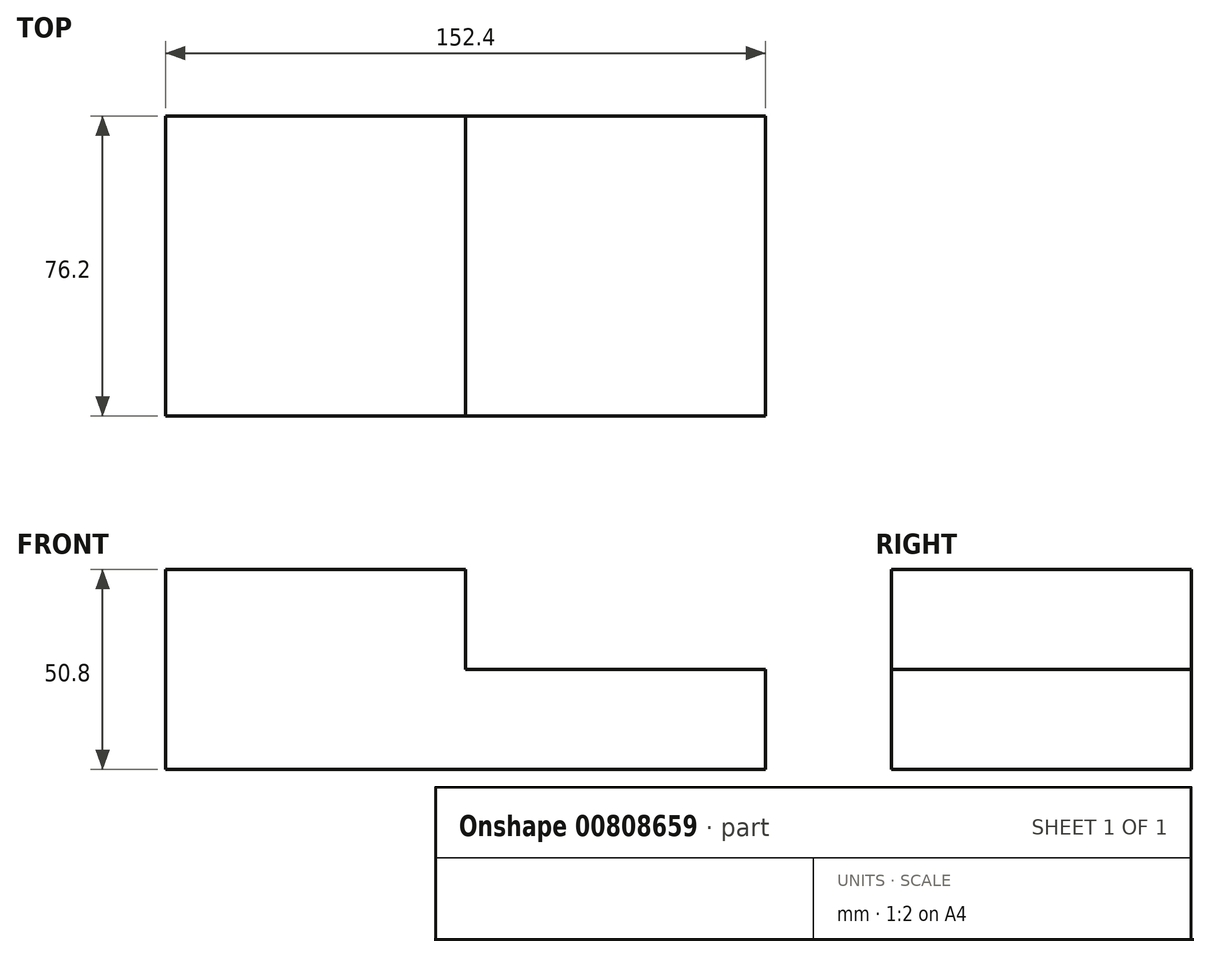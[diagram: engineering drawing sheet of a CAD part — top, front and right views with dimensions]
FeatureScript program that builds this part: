
annotation { "Feature Type Name" : "Feature", "Feature Type Description" : "" }
export const myFeature = defineFeature(function(context is Context, id is Id, definition is map)
    precondition{}
    {
        {
            var Q0;
            Q0=qCreatedBy(makeId("Front.planeOp"),FACE);
            var sketch = newSketch(context, id + "F0", { "sketchPlane" : qUnion([Q0])});
            skLineSegment(sketch, "E0", {"start": v(-72.41, 0) * mm, "end": v(79.99, 0) * mm});
            skLineSegment(sketch, "E1", {"start": v(-72.41, 0) * mm, "end": v(-72.41, 50.8) * mm});
            skLineSegment(sketch, "E2", {"start": v(-72.41, 50.8) * mm, "end": v(3.79, 50.8) * mm});
            skLineSegment(sketch, "E3", {"start": v(3.79, 50.8) * mm, "end": v(3.79, 25.4) * mm});
            skLineSegment(sketch, "E4", {"start": v(3.79, 25.4) * mm, "end": v(79.99, 25.4) * mm});
            skLineSegment(sketch, "E5", {"start": v(79.99, 25.4) * mm, "end": v(79.99, 0) * mm});
            skSolve(sketch);
        }
        {
            var Q0;
            Q0 = qSketchRegion(id + "F0", true);
            extrude(context, id + "F1", {"entities" : qUnion([Q0]), "depth" : 25.4 * mm, "offsetDistance" : 25.4 * mm});
        }
        {
            var Q0;
            Q0=makeQuery(id+"F1.opExtrude","CAP_FACE",FACE,{"disambiguationData":[OSD([sQuery(id+"F0.wireOp",EDGE,"E0"),sQuery(id+"F0.wireOp",EDGE,"E1"),sQuery(id+"F0.wireOp",EDGE,"E2"),sQuery(id+"F0.wireOp",EDGE,"E3"),sQuery(id+"F0.wireOp",EDGE,"E4"),sQuery(id+"F0.wireOp",EDGE,"E5")])],"isStart":false});
            extrude(context, id + "F2", {"entities" : qUnion([Q0]), "operationType" : NewBodyOperationType.ADD, "depth" : 50.8 * mm, "offsetDistance" : 25.4 * mm});
        }
    });
